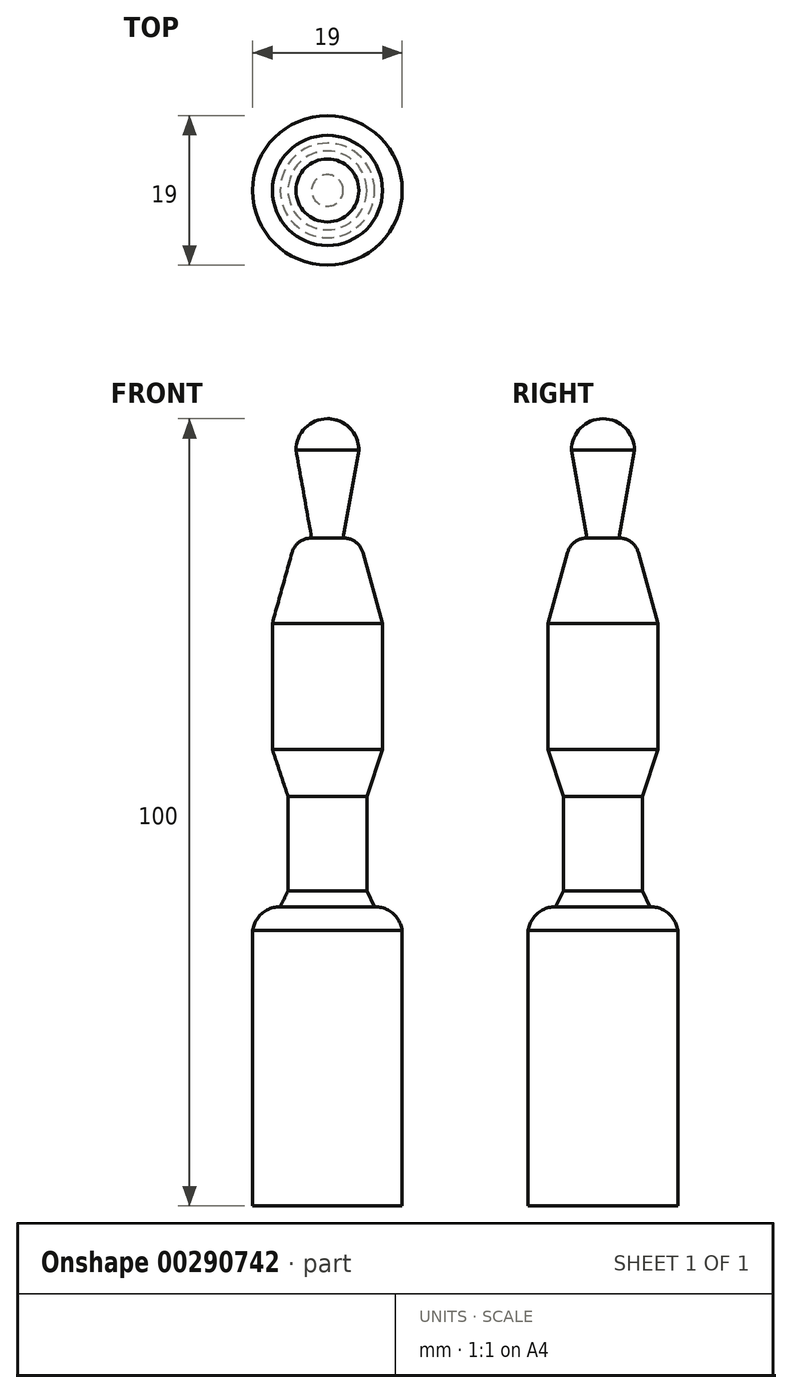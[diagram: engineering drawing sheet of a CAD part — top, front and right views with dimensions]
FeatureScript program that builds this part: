
annotation { "Feature Type Name" : "Feature", "Feature Type Description" : "" }
export const myFeature = defineFeature(function(context is Context, id is Id, definition is map)
    precondition{}
    {
        {
            var Q0;
            Q0=qCreatedBy(makeId("Front.planeOp"),FACE);
            var sketch = newSketch(context, id + "F0", { "sketchPlane" : qUnion([Q0])});
            skArc(sketch, "E0", {"start": v(4, -4) * mm, "mid": v(2.83, -1.17) * mm, "end": v(0, 0) * mm});
            skLineSegment(sketch, "E1", {"start": v(4, -4) * mm, "end": v(2, -15.17) * mm});
            skArc(sketch, "E2", {"start": v(4.5, -17) * mm, "mid": v(3.57, -15.65) * mm, "end": v(2, -15.17) * mm});
            skLineSegment(sketch, "E3", {"start": v(4.5, -17) * mm, "end": v(7, -26) * mm});
            skLineSegment(sketch, "E4", {"start": v(7, -26) * mm, "end": v(7, -42) * mm});
            skLineSegment(sketch, "E5", {"start": v(7, -42) * mm, "end": v(5, -48) * mm});
            skLineSegment(sketch, "E6", {"start": v(5, -48) * mm, "end": v(5, -60) * mm});
            skLineSegment(sketch, "E7", {"start": v(6, -62) * mm, "end": v(5, -60) * mm});
            skArc(sketch, "E8", {"start": v(9.5, -65) * mm, "mid": v(8.31, -62.84) * mm, "end": v(6, -62) * mm});
            skLineSegment(sketch, "E9", {"start": v(9.5, -65) * mm, "end": v(9.5, -100) * mm});
            skLineSegment(sketch, "E10", {"start": v(9.5, -100) * mm, "end": v(0, -100) * mm});
            skLineSegment(sketch, "E11", {"start": v(0, -100) * mm, "end": v(0, 0) * mm});
            skSolve(sketch);
        }
        {
            var Q0;
            Q0=makeQuery(id+"F0.imprint","IMPRINT",FACE,{"disambiguationData":[TD([[makeQuery(id+"F0.imprint","IMPRINT",EDGE,{"derivedFrom":sQuery(id+"F0.wireOp",EDGE,"E0")}),1.0]])]});
            var Q1;
            Q1=sQuery(id+"F0.wireOp",EDGE,"E11");
            revolve(context, id + "F1", {"entities" : qUnion([Q0]), "axis" : qUnion([Q1]), "revolveType" : RevolveType.FULL});
        }
    });
